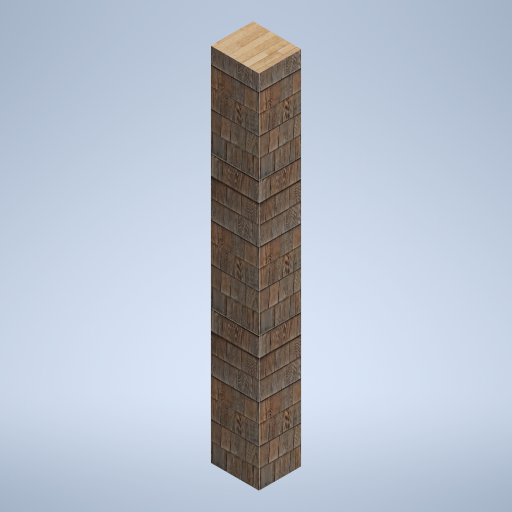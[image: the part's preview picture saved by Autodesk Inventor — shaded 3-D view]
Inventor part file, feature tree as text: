
AUTODESK INVENTOR PART (.ipt)
format: ipt  version: 2024.2 (Build 282272000, 272)  size: 356,864 bytes
history: native  units: mm
features: extrude x1, sketch x1
ambient origin geometry x8: Origin, YZ Plane, XZ Plane, XY Plane, X Axis, Y Axis, Z Axis, Center Point
bodies: Solid1 (feature_tree)
feature tree (2):
  extrude  "Extrusion1"  Depth=350.0mm
  sketch  "Sketch1"  dims[d0=400.0mm d1=350.0mm d2=3000.0mm d3=0.0mm]
